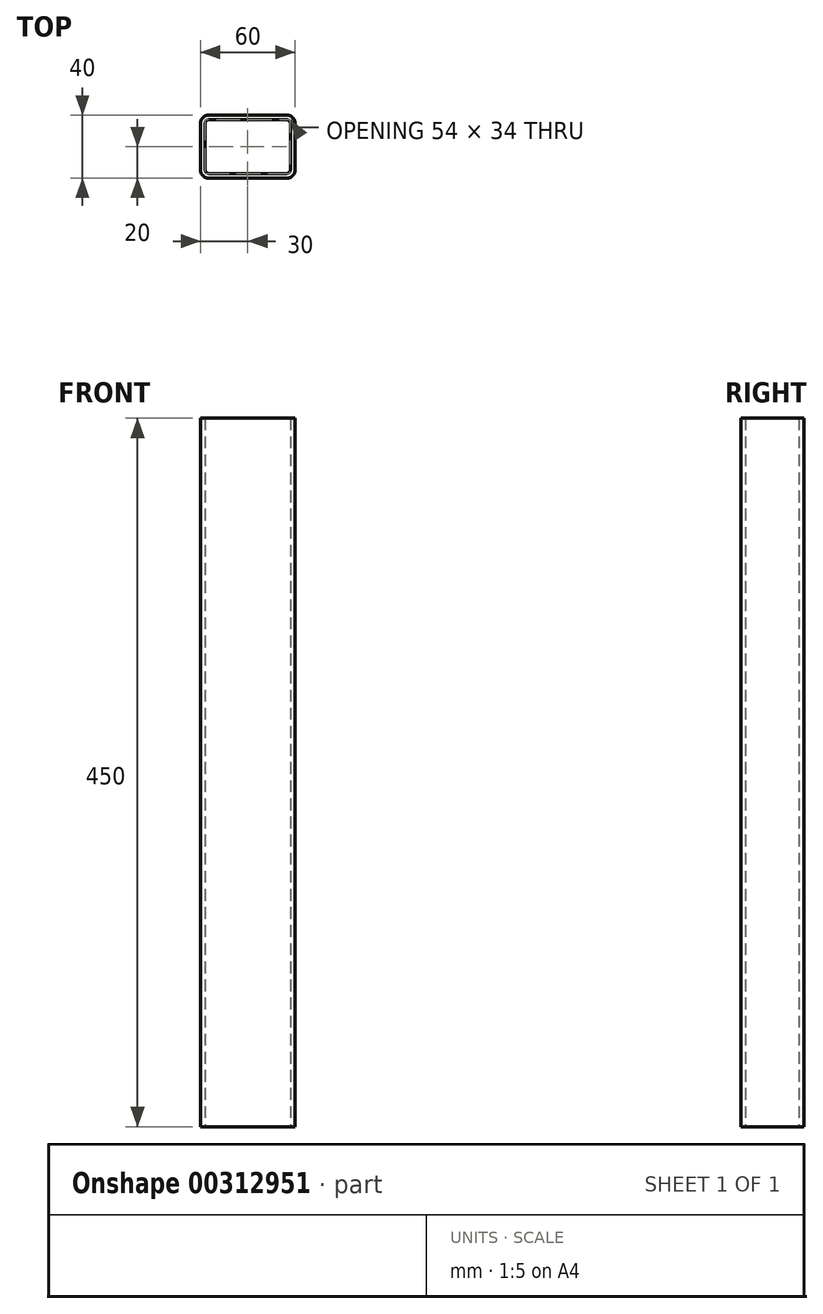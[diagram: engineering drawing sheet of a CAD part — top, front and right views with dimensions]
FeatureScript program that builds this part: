
annotation { "Feature Type Name" : "Feature", "Feature Type Description" : "" }
export const myFeature = defineFeature(function(context is Context, id is Id, definition is map)
    precondition{}
    {
        {
            var Q0;
            Q0=qCreatedBy(makeId("Top.planeOp"),FACE);
            var sketch = newSketch(context, id + "F0", { "sketchPlane" : qUnion([Q0])});
            skLineSegment(sketch, "E0.bottom", {"start": v(25, 20) * mm, "end": v(-25, 20) * mm});
            skLineSegment(sketch, "E0.top", {"start": v(25, -20) * mm, "end": v(-25, -20) * mm});
            skLineSegment(sketch, "E0.left", {"start": v(30, 15) * mm, "end": v(30, -15) * mm});
            skLineSegment(sketch, "E0.right", {"start": v(-30, 15) * mm, "end": v(-30, -15) * mm});
            skPoint(sketch, "E0.middle", {"position": v(0, 0) * mm});
            skLineSegment(sketch, "E1.0", {"start": v(25, 17) * mm, "end": v(-25, 17) * mm});
            skLineSegment(sketch, "E2.0", {"start": v(27, 15) * mm, "end": v(27, -15) * mm});
            skLineSegment(sketch, "E3.0", {"start": v(25, -17) * mm, "end": v(-25, -17) * mm});
            skLineSegment(sketch, "E4.0", {"start": v(-27, 15) * mm, "end": v(-27, -15) * mm});
            skPoint(sketch, "E5.visualSharp", {"position": v(-30, 20) * mm});
            skArc(sketch, "E5.filletArc", {"start": v(-25, 20) * mm, "mid": v(-28.54, 18.54) * mm, "end": v(-30, 15) * mm});
            skPoint(sketch, "E6.visualSharp", {"position": v(30, 20) * mm});
            skArc(sketch, "E6.filletArc", {"start": v(30, 15) * mm, "mid": v(28.54, 18.54) * mm, "end": v(25, 20) * mm});
            skPoint(sketch, "E7.visualSharp", {"position": v(30, -20) * mm});
            skArc(sketch, "E7.filletArc", {"start": v(25, -20) * mm, "mid": v(28.54, -18.54) * mm, "end": v(30, -15) * mm});
            skPoint(sketch, "E8.visualSharp", {"position": v(-30, -20) * mm});
            skArc(sketch, "E8.filletArc", {"start": v(-30, -15) * mm, "mid": v(-28.54, -18.54) * mm, "end": v(-25, -20) * mm});
            skPoint(sketch, "E9.visualSharp", {"position": v(-27, 17) * mm});
            skArc(sketch, "E9.filletArc", {"start": v(-25, 17) * mm, "mid": v(-26.41, 16.41) * mm, "end": v(-27, 15) * mm});
            skPoint(sketch, "E10.visualSharp", {"position": v(27, 17) * mm});
            skArc(sketch, "E10.filletArc", {"start": v(27, 15) * mm, "mid": v(26.41, 16.41) * mm, "end": v(25, 17) * mm});
            skPoint(sketch, "E11.visualSharp", {"position": v(27, -17) * mm});
            skArc(sketch, "E11.filletArc", {"start": v(25, -17) * mm, "mid": v(26.41, -16.41) * mm, "end": v(27, -15) * mm});
            skPoint(sketch, "E12.visualSharp", {"position": v(-27, -17) * mm});
            skArc(sketch, "E12.filletArc", {"start": v(-27, -15) * mm, "mid": v(-26.41, -16.41) * mm, "end": v(-25, -17) * mm});
            skSolve(sketch);
        }
        {
            var Q0;
            Q0=qSketchRegion(id+"F0",true);
            extrude(context, id + "F1", {"entities" : qUnion([Q0]), "depth" : 450 * mm, "offsetDistance" : 25 * mm});
        }
    });
